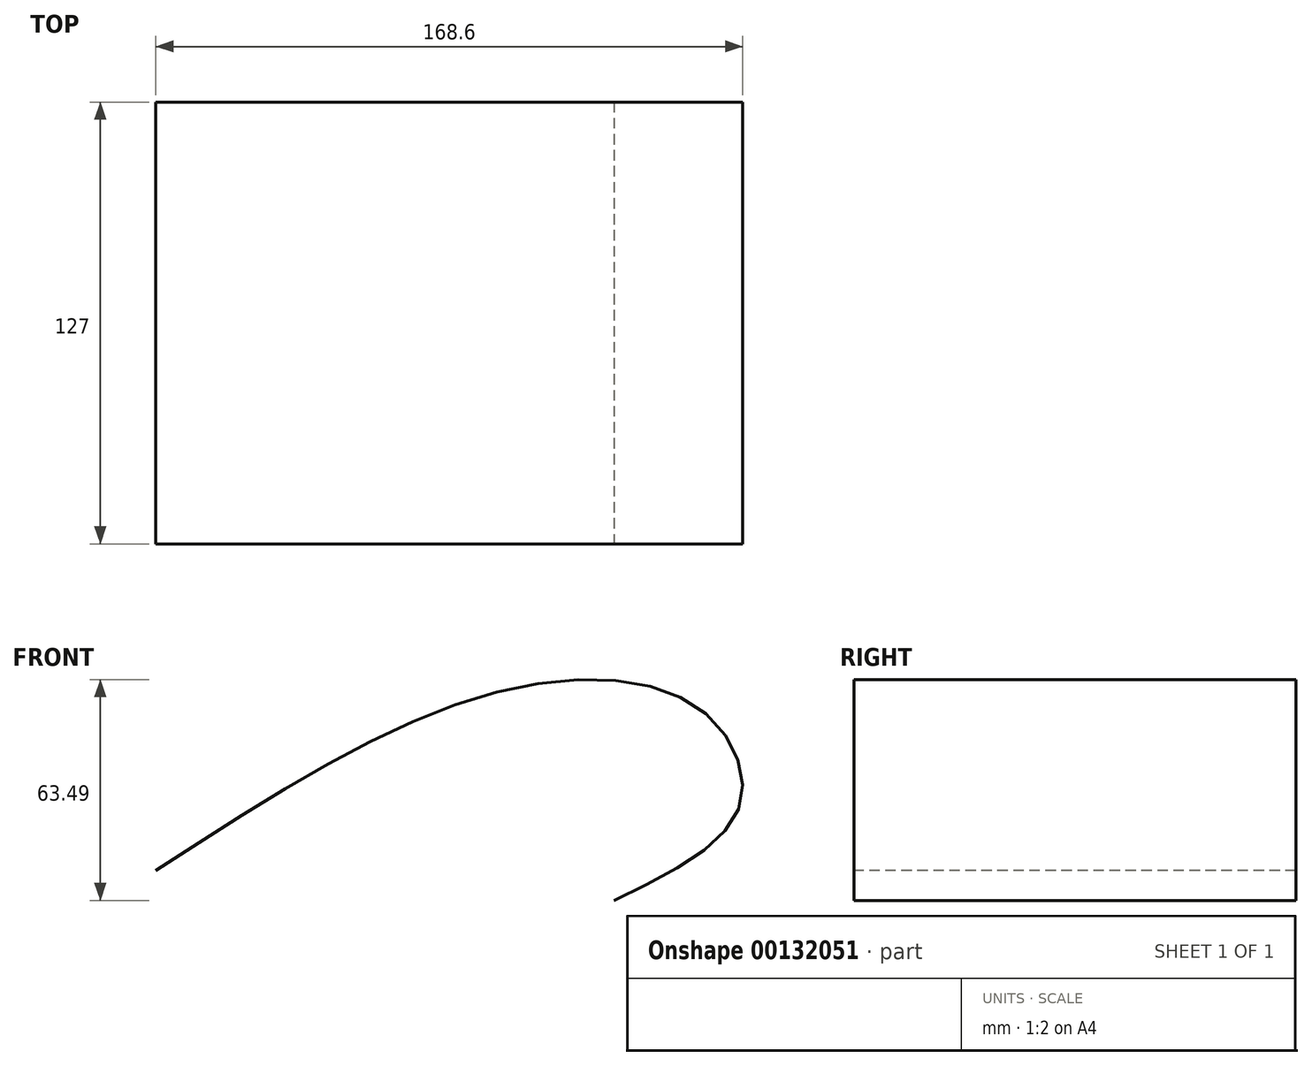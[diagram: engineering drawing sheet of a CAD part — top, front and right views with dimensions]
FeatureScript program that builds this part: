
annotation { "Feature Type Name" : "Feature", "Feature Type Description" : "" }
export const myFeature = defineFeature(function(context is Context, id is Id, definition is map)
    precondition{}
    {
        {
            var Q0;
            Q0=qCreatedBy(makeId("Front.planeOp"),FACE);
            var sketch = newSketch(context, id + "F0", { "sketchPlane" : qUnion([Q0])});
            skFitSpline(sketch, "E0", {"points": [v(0, 0) * mm, v(35.98, 26.67) * mm, v(24.9, 54.85) * mm, v(-34.47, 59.63) * mm, v(-131.59, 8.55) * mm], "startDerivative": vector(217.81, 104.63) * mm, "endDerivative": vector(-285, -185.95) * mm});
            skSolve(sketch);
        }
        {
            var Q0;
            Q0=sQuery(id+"F0.wireOp",EDGE,"E0");
            extrude(context, id + "F1", {"bodyType" : ToolBodyType.SURFACE, "surfaceEntities" : qUnion([Q0]), "depth" : 127 * mm});
        }
    });
